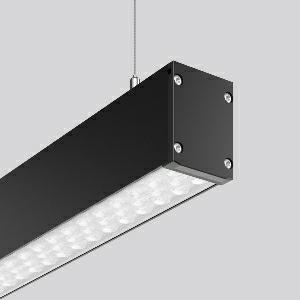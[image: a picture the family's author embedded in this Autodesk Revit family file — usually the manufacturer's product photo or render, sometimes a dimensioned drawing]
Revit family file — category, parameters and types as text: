
# Revit family: linedo_single_ip54_312565_003_1_c6e1
name_source: partatom
category: Lighting Fixtures
units: mm (PartAtom-declared; Revit-internal decimal feet)

## family parameters
Cut with Voids When Loaded = No
Host = Face
Light Source = No
Part Type = Normal
Room Calculation Point = No
Round Connector Dimension = Use Diameter
Shared = No

## types (1)
- LINEDO single IP54 (1 x LED Modul 840, 4850 lm, 4000)
    Apparent Load = 31 VA
    CIE Flux Codes = 86 96 99 100 100
    Color Rendering = 80
    Color Temperature = 4000
    Default Elevation = 1800 mm
    Description = Series: LINEDO single IP54
Stylish pendant luminaire. Housing: extruded aluminium profile, powder-coated. Plastic end caps, black. High-efficiency LED units with optimum light control thanks to clear plastic (PC) lens optics. 2-point steel cable suspension freely positionable and infinitely height-adjustable. With power cord (2.5 m). Please order canopy separately if required. Perfect for office areas (RUG < 19) and environments with computer screens in accordance with EN 12464-1. Luminaire with limited surface temperature in accordance with EN 60598-2-24 for use in environments in which a deposit of conductive dust on the luminaire can be expected. 
Colour: jet black (RAL 9005)
Length: 1710 mm
Width: 58 mm
Height: 76 mm
Suspension length: 100-1500 mm
Lamp: LED
Socket: without socket
Colour temperature: 4000K
Colour rendering index (CRI): 80
System power: 31 W
Rated luminous flux: 4850 lm
Beam angle Down: 59°
Luminous efficiency: 156 lm/W
Control gear: Regulated power supply
Protection class: I
Type of protection: IP 54
    Height = 76 mm
    Lamp = 1 x LED Modul 840
    Lamp Light Flux = 4850 lm
    Lamp count = 1
    Length = 1710 mm
    Lifetime = 50000 h
    Luminous efficacy = 156 lm/W
    Manufacturer = RZB
    ModVariant = No
    Model = 312565.003.1
    Mounting Place = Ceiling
    Mounting Type = Surface mounted, Pendant
    Number of Poles = 1
    OnlyDefault = Yes
    Power Factor = 1
    Product Name = LINEDO single IP54
    Product group = Pendant luminaires
    ProductGroupID = 902
    Protection Class = Protection class I
    Protection Degree = IP 54
    RLX_Detail_Level = 1
    RLX_Emergency_Light_Flux = 0 lm
    RLX_Emergency_Type = 0
    RLX_Emergency_Type_DB = No
    RlxData = <blob elided: 35925 chars, md5=4c046e7c>
    Socket = socket
    Standby Power = 0 W
    System Light Flux = 4850 lm
    System Power = 31 W
    Type Comments = ALEA SPOT
    Type Image = 312565.003.jpg
    URL = http://relux.com
    VarID = ---
    Voltage = 230 V
    Voltage Range = 220-240 V
    Weight = 0.00 kg
    Width = 58 mm

## geometry (parser evidence)
native form markers: Blend x4, Sweep x9
no freeform markers — native parametric forms only
